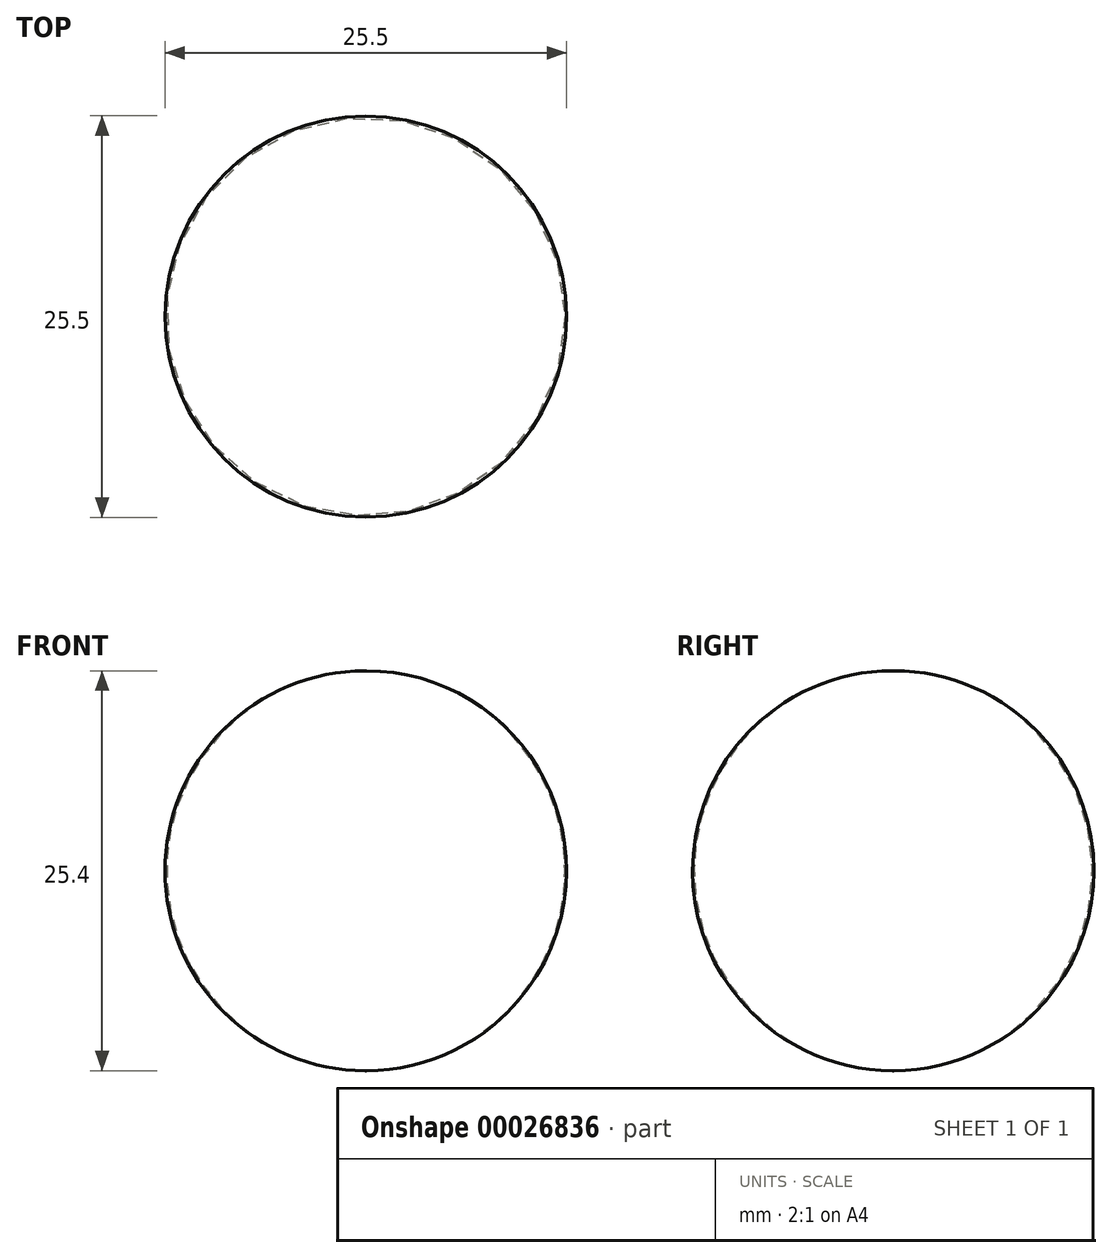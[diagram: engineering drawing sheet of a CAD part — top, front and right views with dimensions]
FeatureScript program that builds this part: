
annotation { "Feature Type Name" : "Feature", "Feature Type Description" : "" }
export const myFeature = defineFeature(function(context is Context, id is Id, definition is map)
    precondition{}
    {
        {
            var Q0;
            Q0=qCreatedBy(makeId("Front.planeOp"),FACE);
            var sketch = newSketch(context, id + "F0", { "sketchPlane" : qUnion([Q0])});
            skLineSegment(sketch, "E0", {"start": v(0, 0) * mm, "end": v(0, 25.4) * mm});
            skArc(sketch, "E1", {"start": v(0, 0) * mm, "mid": v(12.75, 12.7) * mm, "end": v(0, 25.4) * mm});
            skSolve(sketch);
        }
        {
            var Q0;
            Q0=makeQuery(id+"F0.imprint","IMPRINT",FACE,{"disambiguationData":[TD([[makeQuery(id+"F0.imprint","IMPRINT",EDGE,{"derivedFrom":sQuery(id+"F0.wireOp",EDGE,"E0")}),-1.0]])]});
            var Q1;
            Q1=sQuery(id+"F0.wireOp",EDGE,"E0");
            revolve(context, id + "F1", {"entities" : qUnion([Q0]), "axis" : qUnion([Q1]), "revolveType" : RevolveType.FULL});
        }
    });
